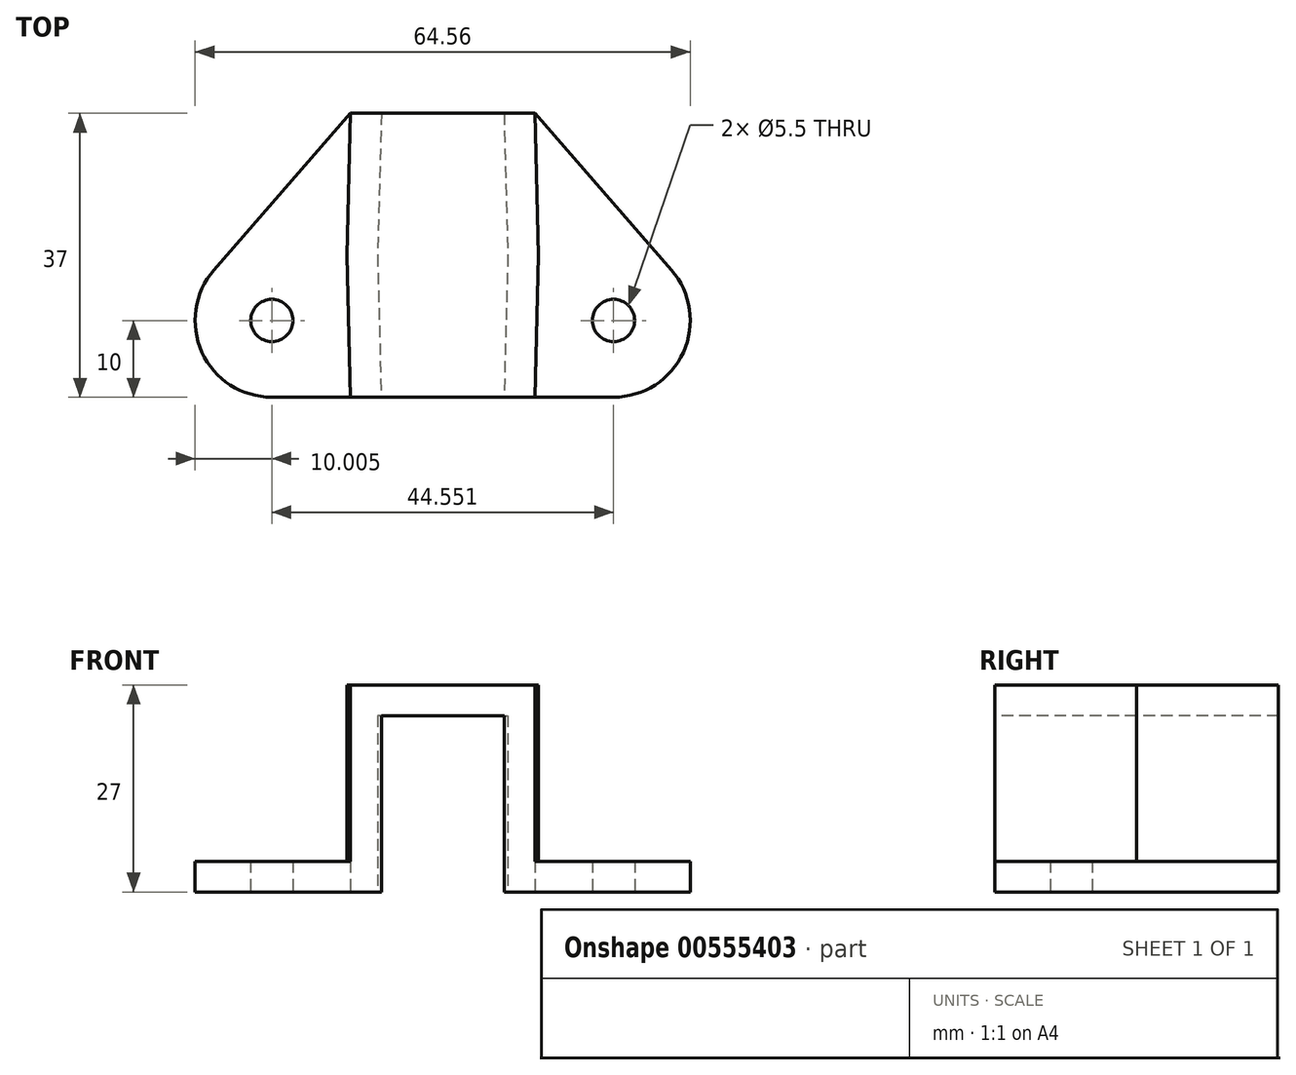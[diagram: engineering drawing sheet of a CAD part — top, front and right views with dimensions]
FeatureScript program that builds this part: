
annotation { "Feature Type Name" : "Feature", "Feature Type Description" : "" }
export const myFeature = defineFeature(function(context is Context, id is Id, definition is map)
    precondition{}
    {
        {
            var Q0;
            Q0=qCreatedBy(makeId("Top.planeOp"),FACE);
            var sketch = newSketch(context, id + "F0", { "sketchPlane" : qUnion([Q0])});
            skLineSegment(sketch, "E0", {"start": v(-22.28, 0) * mm, "end": v(22.28, 0) * mm});
            skLineSegment(sketch, "E1", {"start": v(12, 37) * mm, "end": v(-12, 37) * mm});
            skLineSegment(sketch, "E2", {"start": v(-12, 37) * mm, "end": v(-29.81, 16.57) * mm});
            skLineSegment(sketch, "E3", {"start": v(0, 0) * mm, "end": v(0, 37) * mm, "construction": true});
            skArc(sketch, "E4", {"start": v(-29.81, 16.57) * mm, "mid": v(-31.38, 5.86) * mm, "end": v(-22.28, 0) * mm});
            skLineSegment(sketch, "E5.MirrorCS", {"start": v(12, 37) * mm, "end": v(29.81, 16.57) * mm});
            skArc(sketch, "E6.MirrorCS", {"start": v(29.81, 16.57) * mm, "mid": v(31.38, 5.86) * mm, "end": v(22.28, 0) * mm});
            skCircle(sketch, "E7", {"center": v(-22.28, 10) * mm, "radius": 2.75 * mm});
            skCircle(sketch, "E8", {"center": v(22.28, 10) * mm, "radius": 2.75 * mm});
            skLineSegment(sketch, "E9", {"start": v(-8, 37) * mm, "end": v(-8.5, 18.5) * mm});
            skLineSegment(sketch, "E10", {"start": v(-8.5, 18.5) * mm, "end": v(-8, 0) * mm});
            skLineSegment(sketch, "E11", {"start": v(-8.5, 18.5) * mm, "end": v(8.5, 18.5) * mm, "construction": true});
            skPoint(sketch, "E12", {"position": v(0, 18.5) * mm});
            skLineSegment(sketch, "E13.MirrorCS", {"start": v(8.5, 18.5) * mm, "end": v(8, 0) * mm});
            skLineSegment(sketch, "E14.MirrorCS", {"start": v(8, 37) * mm, "end": v(8.5, 18.5) * mm});
            skLineSegment(sketch, "E15", {"start": v(-12, 0) * mm, "end": v(-12.5, 18.5) * mm});
            skLineSegment(sketch, "E16", {"start": v(-12.5, 18.5) * mm, "end": v(-12, 37) * mm});
            skLineSegment(sketch, "E17.MirrorCS", {"start": v(12.5, 18.5) * mm, "end": v(12, 37) * mm});
            skLineSegment(sketch, "E18.MirrorCS", {"start": v(12, 0) * mm, "end": v(12.5, 18.5) * mm});
            skPoint(sketch, "E19.visualSharp", {"position": v(-8.5, 18.5) * mm});
            skCircle(sketch, "E20", {"center": v(22.28, 10) * mm, "radius": 10 * mm, "construction": true});
            skSolve(sketch);
        }
        {
            var Q0;
            Q0=makeQuery(id+"F0.imprint","IMPRINT",FACE,{"disambiguationData":[TD([[makeQuery(id+"F0.imprint","IMPRINT",EDGE,{"derivedFrom":sQuery(id+"F0.wireOp",EDGE,"E5.MirrorCS")}),-1.0]])]});
            var Q1;
            Q1=makeQuery(id+"F0.imprint","IMPRINT",FACE,{"disambiguationData":[TD([[makeQuery(id+"F0.imprint","IMPRINT",EDGE,{"derivedFrom":sQuery(id+"F0.wireOp",EDGE,"E2")}),1.0]])]});
            extrude(context, id + "F1", {"entities" : qUnion([Q0, Q1]), "depth" : 4 * mm, "offsetDistance" : 25 * mm});
        }
        {
            var Q0;
            {var subQ1=sQuery(id+"F0.wireOp",EDGE,"E9");Q0=makeQuery(id+"F0.imprint","IMPRINT",FACE,{"disambiguationData":[TD([[makeQuery(id+"F0.imprint","IMPRINT",EDGE,{"derivedFrom":subQ1}),-1.0]])]});}
            var Q1;
            {var subQ1=sQuery(id+"F0.wireOp",EDGE,"E13.MirrorCS");Q1=makeQuery(id+"F0.imprint","IMPRINT",FACE,{"disambiguationData":[TD([[makeQuery(id+"F0.imprint","IMPRINT",EDGE,{"derivedFrom":subQ1}),1.0]])]});}
            extrude(context, id + "F2", {"entities" : qUnion([Q0, Q1]), "operationType" : NewBodyOperationType.ADD, "depth" : 23 * mm, "offsetDistance" : 25 * mm});
        }
        {
            var Q0;
            {var subQ1=sQuery(id+"F0.wireOp",EDGE,"E9");Q0=makeQuery(id+"F0.imprint","IMPRINT",FACE,{"disambiguationData":[TD([[makeQuery(id+"F0.imprint","IMPRINT",EDGE,{"derivedFrom":subQ1}),1.0]])]});}
            var Q1;
            {var subQ1=sQuery(id+"F0.wireOp",EDGE,"E9");Q1=makeQuery(id+"F0.imprint","IMPRINT",FACE,{"disambiguationData":[TD([[makeQuery(id+"F0.imprint","IMPRINT",EDGE,{"derivedFrom":subQ1}),-1.0]])]});}
            var Q2;
            {var subQ1=sQuery(id+"F0.wireOp",EDGE,"E13.MirrorCS");Q2=makeQuery(id+"F0.imprint","IMPRINT",FACE,{"disambiguationData":[TD([[makeQuery(id+"F0.imprint","IMPRINT",EDGE,{"derivedFrom":subQ1}),1.0]])]});}
            extrude(context, id + "F3", {"entities" : qUnion([Q0, Q1, Q2]), "operationType" : NewBodyOperationType.ADD, "depth" : 27 * mm, "offsetDistance" : 25 * mm, "hasSecondDirection" : true, "secondDirectionOppositeDirection" : false, "secondDirectionDepth" : 23 * mm});
        }
    });
